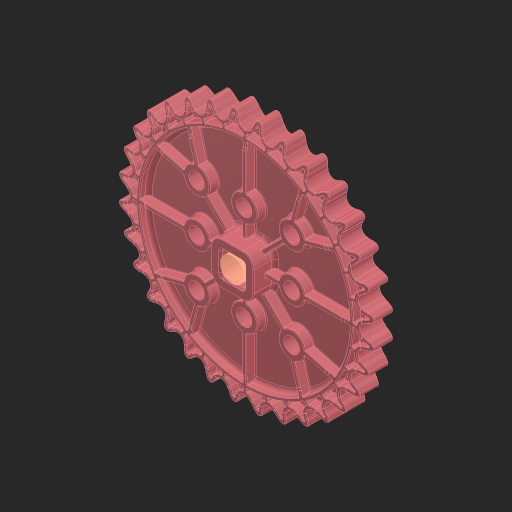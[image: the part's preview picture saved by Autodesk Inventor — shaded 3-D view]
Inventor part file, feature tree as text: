
AUTODESK INVENTOR PART (.ipt)
format: ipt  version: 2023 (Build 270158000, 158)  size: 9,829,888 bytes
history: native  units: in
note: dims shown in document units (in); Inventor stores cm internally (conversion verified against a paired STEP export)
features: sketch x1, other x1, mirror x1, extrude x1
ambient origin geometry x8: Origin, YZ Plane, XZ Plane, XY Plane, X Axis, Y Axis, Z Axis, Center Point
bodies: Solid1 (feature_tree)
feature tree (4):
  sketch  "Sketch1"  dims[d0=0.25in d1=0.3937in d2=0.0in]
  other  "Srf1"
  mirror  "Mirror1"
  extrude  "ExtrusionSrf1"  Depth=0.3937in TaperAngle=0.0deg
